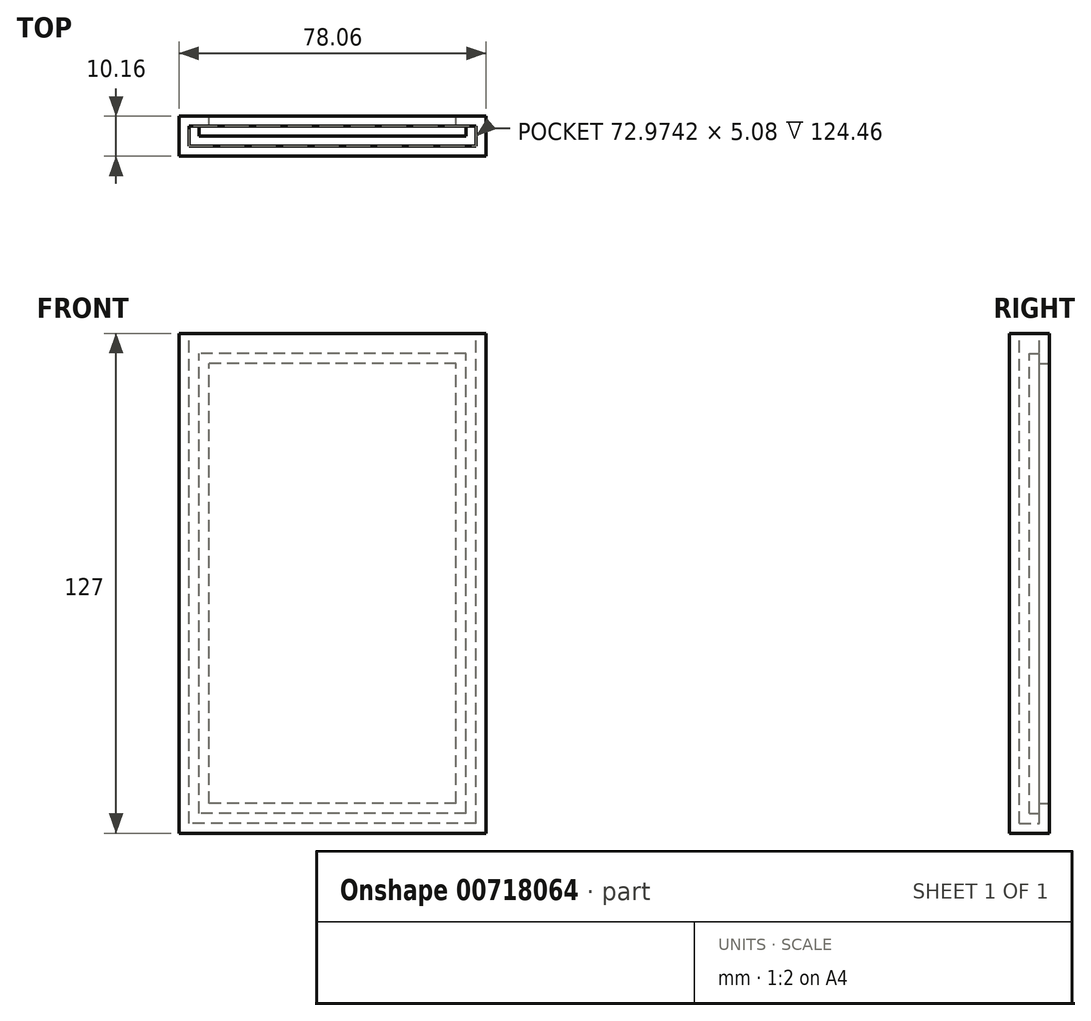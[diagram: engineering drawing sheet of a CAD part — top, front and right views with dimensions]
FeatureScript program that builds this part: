
annotation { "Feature Type Name" : "Feature", "Feature Type Description" : "" }
export const myFeature = defineFeature(function(context is Context, id is Id, definition is map)
    precondition{}
    {
        {
            var Q0;
            Q0=qCreatedBy(makeId("Front.planeOp"),FACE);
            var sketch = newSketch(context, id + "F0", { "sketchPlane" : qUnion([Q0])});
            skLineSegment(sketch, "E0.bottom", {"start": v(39.03, -63.5) * mm, "end": v(-39.03, -63.5) * mm});
            skLineSegment(sketch, "E0.top", {"start": v(39.03, 63.5) * mm, "end": v(-39.03, 63.5) * mm});
            skLineSegment(sketch, "E0.left", {"start": v(39.03, -63.5) * mm, "end": v(39.03, 63.5) * mm});
            skLineSegment(sketch, "E0.right", {"start": v(-39.03, -63.5) * mm, "end": v(-39.03, 63.5) * mm});
            skPoint(sketch, "E0.middle", {"position": v(0, 0) * mm});
            skSolve(sketch);
        }
        {
            var Q0;
            Q0=qSketchRegion(id+"F0",true);
            extrude(context, id + "F1", {"entities" : qUnion([Q0]), "depth" : 10.16 * mm, "offsetDistance" : 25.4 * mm});
        }
        {
            var Q0;
            Q0=makeQuery(id+"F1.opExtrude","CAP_FACE",FACE,{"disambiguationData":[OSD([sQuery(id+"F0.wireOp",EDGE,"E0.bottom"),sQuery(id+"F0.wireOp",EDGE,"E0.top"),sQuery(id+"F0.wireOp",EDGE,"E0.left"),sQuery(id+"F0.wireOp",EDGE,"E0.right")])],"isStart":true});
            shell(context, id + "F2", {"entities" : qUnion([Q0]), "thickness" : 7.62 * mm});
        }
        {
            var Q0;
            Q0=makeQuery(id+"F1.opExtrude","SWEPT_FACE",FACE,{"disambiguationData":[OSD([sQuery(id+"F0.wireOp",EDGE,"E0.top")])]});
            shell(context, id + "F3", {"entities" : qUnion([Q0]), "thickness" : 2.54 * mm});
        }
    });
